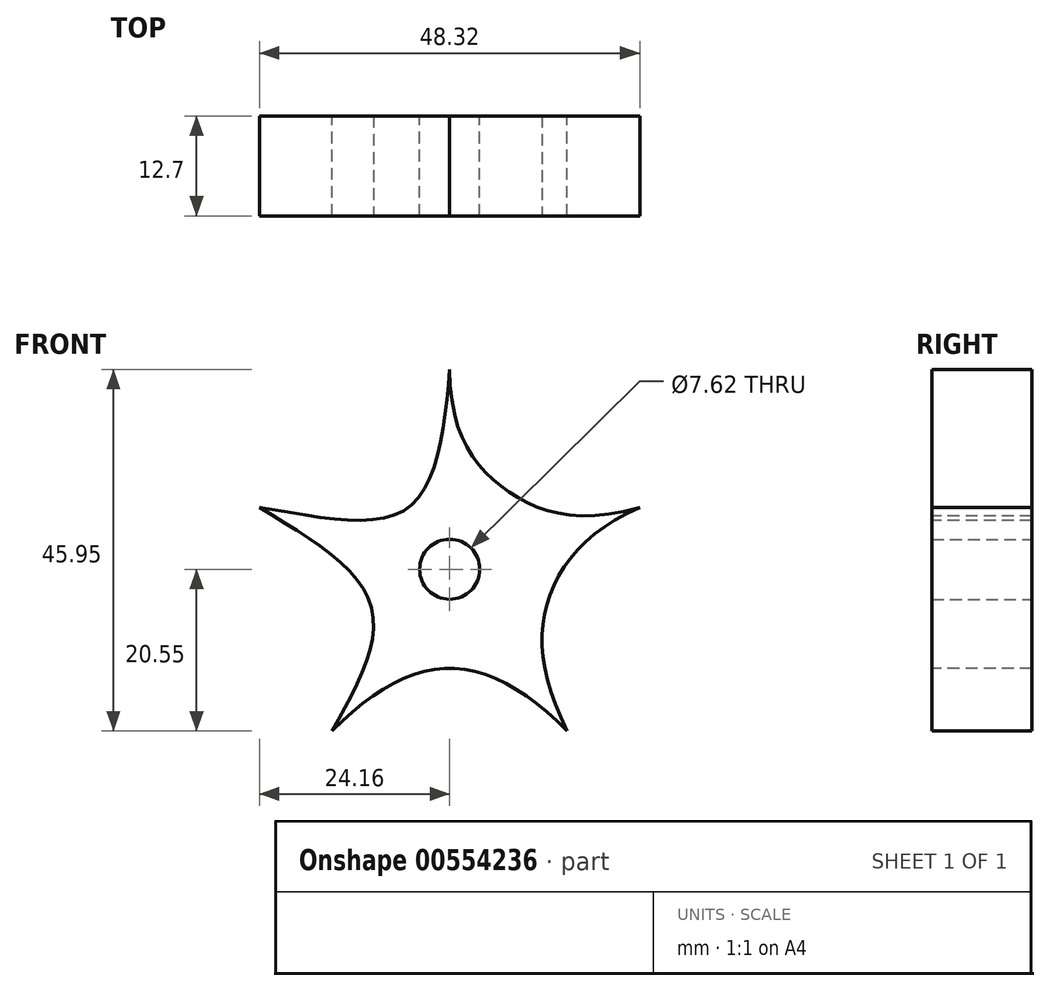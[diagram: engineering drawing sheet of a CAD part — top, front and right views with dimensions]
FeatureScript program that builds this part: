
annotation { "Feature Type Name" : "Feature", "Feature Type Description" : "" }
export const myFeature = defineFeature(function(context is Context, id is Id, definition is map)
    precondition{}
    {
        {
            var Q0;
            Q0=qCreatedBy(makeId("Front.planeOp"),FACE);
            var sketch = newSketch(context, id + "F0", { "sketchPlane" : qUnion([Q0])});
            skCircle(sketch, "E0", {"center": v(0, 0) * mm, "radius": 25.4 * mm});
            skLineSegment(sketch, "E1", {"start": v(0, 0) * mm, "end": v(24.16, 7.85) * mm});
            skLineSegment(sketch, "E2", {"start": v(0, 0) * mm, "end": v(14.93, -20.55) * mm});
            skLineSegment(sketch, "E3", {"start": v(0, 0) * mm, "end": v(-14.93, -20.55) * mm});
            skLineSegment(sketch, "E4", {"start": v(0, 0) * mm, "end": v(0, 25.4) * mm});
            skLineSegment(sketch, "E5", {"start": v(0, 0) * mm, "end": v(-24.16, 7.85) * mm});
            skFitSpline(sketch, "E6", {"points": [v(-24.16, 7.85) * mm, v(-5.25, 7.85) * mm, v(0, 25.4) * mm], "startDerivative": vector(46.06, -7.43) * mm, "endDerivative": vector(3.9, 44.16) * mm});
            skFitSpline(sketch, "E7", {"points": [v(0, 25.4) * mm, v(6.88, 10.28) * mm, v(24.16, 7.85) * mm], "startDerivative": vector(0.23, -48.9) * mm, "endDerivative": vector(47.95, 13.63) * mm});
            skFitSpline(sketch, "E8", {"points": [v(24.16, 7.85) * mm, v(12.6, -3.7) * mm, v(14.93, -20.55) * mm], "startDerivative": vector(-38.98, -16.74) * mm, "endDerivative": vector(20.1, -39.9) * mm});
            skFitSpline(sketch, "E9", {"points": [v(14.93, -20.55) * mm, v(0, -12.59) * mm, v(-14.93, -20.55) * mm], "startDerivative": vector(-29.86, 30.3) * mm, "endDerivative": vector(-29.86, -30.3) * mm});
            skFitSpline(sketch, "E10", {"points": [v(-14.93, -20.55) * mm, v(-9.95, -4.77) * mm, v(-24.16, 7.85) * mm], "startDerivative": vector(19.43, 34.7) * mm, "endDerivative": vector(-37.23, 22.24) * mm});
            skSolve(sketch);
        }
        {
            var Q0;
            Q0=makeQuery(id+"F0.imprint","IMPRINT",FACE,{"disambiguationData":[TD([[makeQuery(id+"F0.imprint","IMPRINT",EDGE,{"derivedFrom":sQuery(id+"F0.wireOp",EDGE,"E4")}),1.0]])]});
            var Q1;
            Q1=makeQuery(id+"F0.imprint","IMPRINT",FACE,{"disambiguationData":[TD([[makeQuery(id+"F0.imprint","IMPRINT",EDGE,{"derivedFrom":sQuery(id+"F0.wireOp",EDGE,"E1")}),1.0]])]});
            var Q2;
            Q2=makeQuery(id+"F0.imprint","IMPRINT",FACE,{"disambiguationData":[TD([[makeQuery(id+"F0.imprint","IMPRINT",EDGE,{"derivedFrom":sQuery(id+"F0.wireOp",EDGE,"E1")}),-1.0]])]});
            var Q3;
            Q3=makeQuery(id+"F0.imprint","IMPRINT",FACE,{"disambiguationData":[TD([[makeQuery(id+"F0.imprint","IMPRINT",EDGE,{"derivedFrom":sQuery(id+"F0.wireOp",EDGE,"E2")}),-1.0]])]});
            var Q4;
            Q4=makeQuery(id+"F0.imprint","IMPRINT",FACE,{"disambiguationData":[TD([[makeQuery(id+"F0.imprint","IMPRINT",EDGE,{"derivedFrom":sQuery(id+"F0.wireOp",EDGE,"E3")}),-1.0]])]});
            extrude(context, id + "F1", {"entities" : qUnion([Q0, Q1, Q2, Q3, Q4]), "endBound" : BoundingType.SYMMETRIC, "depth" : 12.7 * mm, "offsetDistance" : 25.4 * mm});
        }
        {
            var Q0;
            Q0=sQuery(id+"F0.wireOp",VERTEX,"E5.start");
            var Q1;
            Q1=makeQuery(id+"F1.opExtrude","SWEPT_BODY",BODY,{"disambiguationData":[OSD([sQuery(id+"F0.wireOp",EDGE,"E6"),sQuery(id+"F0.wireOp",EDGE,"E7"),sQuery(id+"F0.wireOp",EDGE,"E8"),sQuery(id+"F0.wireOp",EDGE,"E9"),sQuery(id+"F0.wireOp",EDGE,"E10")])]});
            hole(context, id + "F2", {"style" : HoleStyle.SIMPLE, "endStyle" : HoleEndStyle.THROUGH, "oppositeDirection" : true, "holeDiameter" : 7.62 * mm, "isTappedThrough" : true, "tappedDepth" : 12.7 * mm, "tapClearance" : 3, "locations" : qUnion([Q0]), "scope" : qUnion([Q1])});
        }
        {
            var Q0;
            Q0=sQuery(id+"F0.wireOp",VERTEX,"E5.start");
            var Q1;
            Q1=makeQuery(id+"F1.opExtrude","SWEPT_BODY",BODY,{"disambiguationData":[OSD([sQuery(id+"F0.wireOp",EDGE,"E6"),sQuery(id+"F0.wireOp",EDGE,"E7"),sQuery(id+"F0.wireOp",EDGE,"E8"),sQuery(id+"F0.wireOp",EDGE,"E9"),sQuery(id+"F0.wireOp",EDGE,"E10")])]});
            hole(context, id + "F3", {"style" : HoleStyle.SIMPLE, "endStyle" : HoleEndStyle.THROUGH, "holeDiameter" : 7.62 * mm, "isTappedThrough" : true, "tappedDepth" : 12.7 * mm, "tapClearance" : 3, "locations" : qUnion([Q0]), "scope" : qUnion([Q1])});
        }
    });
